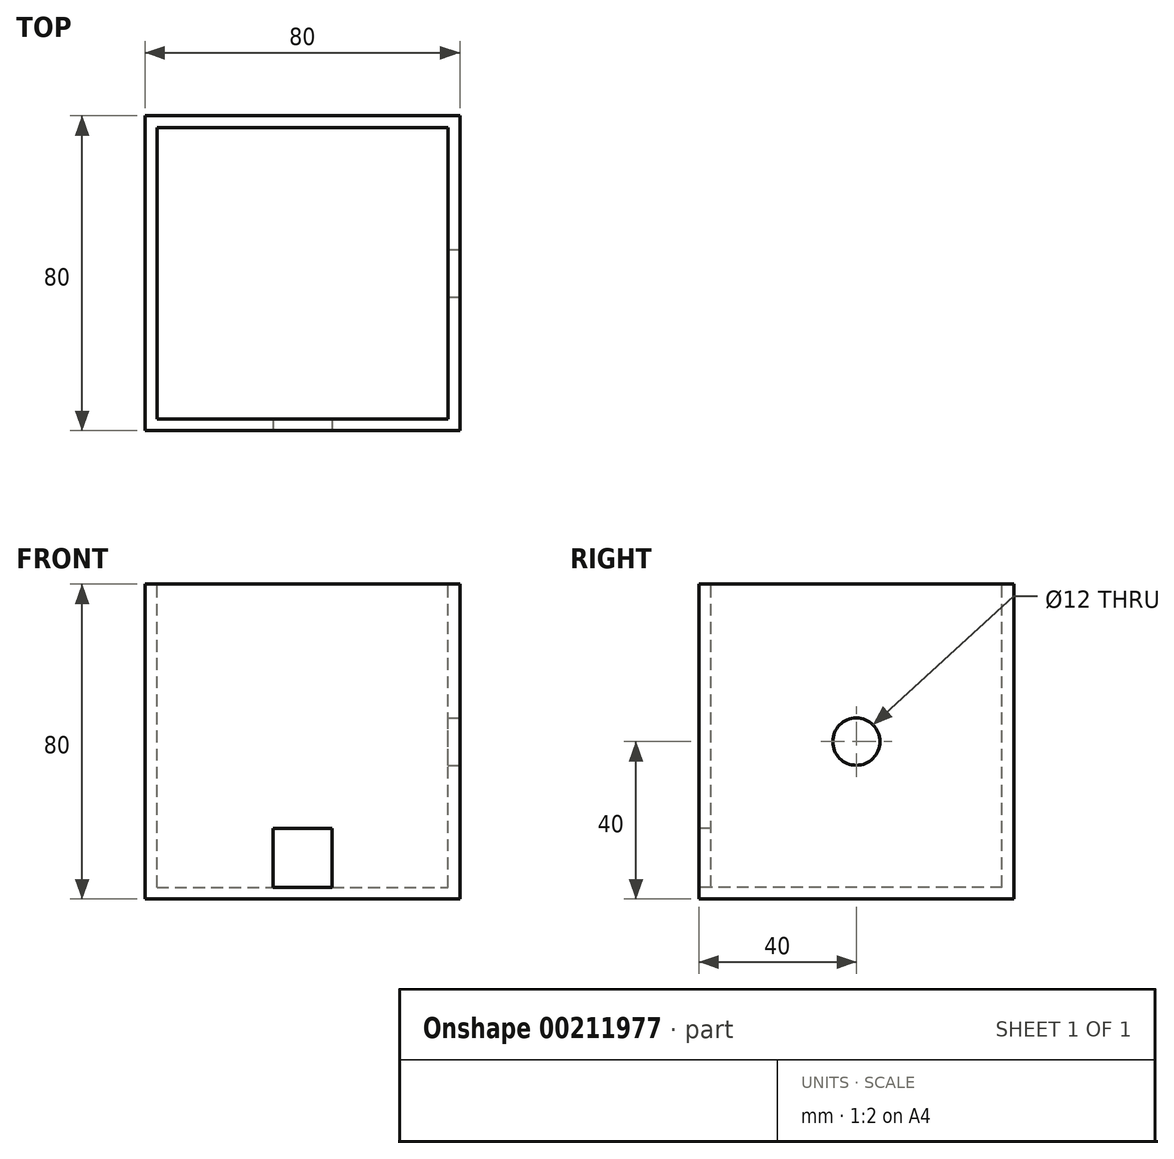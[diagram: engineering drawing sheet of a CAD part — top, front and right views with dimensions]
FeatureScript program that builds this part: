
annotation { "Feature Type Name" : "Feature", "Feature Type Description" : "" }
export const myFeature = defineFeature(function(context is Context, id is Id, definition is map)
    precondition{}
    {
        {
            var Q0;
            Q0=qCreatedBy(makeId("Front.planeOp"),FACE);
            var sketch = newSketch(context, id + "F0", { "sketchPlane" : qUnion([Q0])});
            skLineSegment(sketch, "E0.bottom", {"start": v(-40, -40) * mm, "end": v(40, -40) * mm});
            skLineSegment(sketch, "E0.top", {"start": v(-40, 40) * mm, "end": v(40, 40) * mm});
            skLineSegment(sketch, "E0.left", {"start": v(-40, -40) * mm, "end": v(-40, 40) * mm});
            skLineSegment(sketch, "E0.right", {"start": v(40, -40) * mm, "end": v(40, 40) * mm});
            skPoint(sketch, "E0.middle", {"position": v(0, 0) * mm});
            skSolve(sketch);
        }
        {
            var Q0;
            Q0 = qSketchRegion(id + "F0", true);
            extrude(context, id + "F1", {"entities" : qUnion([Q0]), "depth" : 3 * mm});
        }
        {
            var Q0;
            Q0=makeQuery(id+"F1.opExtrude","CAP_FACE",FACE,{"disambiguationData":[OSD([sQuery(id+"F0.wireOp",EDGE,"E0.bottom"),sQuery(id+"F0.wireOp",EDGE,"E0.top"),sQuery(id+"F0.wireOp",EDGE,"E0.left"),sQuery(id+"F0.wireOp",EDGE,"E0.right")])],"isStart":true});
            var sketch = newSketch(context, id + "F2", { "sketchPlane" : qUnion([Q0])});
            skLineSegment(sketch, "E1.bottom", {"start": v(40, -40) * mm, "end": v(-40, -40) * mm});
            skLineSegment(sketch, "E1.left", {"start": v(40, -40) * mm, "end": v(40, 40) * mm});
            skLineSegment(sketch, "E1.right", {"start": v(-40, -40) * mm, "end": v(-40, 40) * mm});
            skPoint(sketch, "E1.middle", {"position": v(0, 0) * mm});
            skLineSegment(sketch, "E2.bottom", {"start": v(37, -37) * mm, "end": v(-37, -37) * mm});
            skLineSegment(sketch, "E2.left", {"start": v(37, -37) * mm, "end": v(37, 37) * mm});
            skLineSegment(sketch, "E2.right", {"start": v(-37, -37) * mm, "end": v(-37, 37) * mm});
            skLineSegment(sketch, "E3", {"start": v(-37, 37) * mm, "end": v(-37, 40) * mm});
            skLineSegment(sketch, "E4", {"start": v(37, 37) * mm, "end": v(37, 40) * mm});
            skSolve(sketch);
        }
        {
            var Q0;
            Q0 = qSketchRegion(id + "F2", true);
            var Q1;
            Q1=makeQuery(id+"F2.imprint","IMPRINT",FACE,{"disambiguationData":[TD([[makeQuery(id+"F2.imprint","IMPRINT",EDGE,{"derivedFrom":sQuery(id+"F2.wireOp",EDGE,"E1.bottom")}),-1.0]])]});
            extrude(context, id + "F3", {"entities" : qUnion([Q0, Q1]), "operationType" : NewBodyOperationType.ADD, "depth" : (80 - 6) * mm});
        }
        {
            var Q0;
            Q0=makeQuery(id+"F3.opExtrude","CAP_FACE",FACE,{"disambiguationData":[OSD([sQuery(id+"F0.wireOp",EDGE,"E0.top"),sQuery(id+"F2.wireOp",EDGE,"E1.bottom"),sQuery(id+"F2.wireOp",EDGE,"E1.left"),sQuery(id+"F2.wireOp",EDGE,"E1.right"),sQuery(id+"F2.wireOp",EDGE,"E2.bottom"),sQuery(id+"F2.wireOp",EDGE,"E2.left"),sQuery(id+"F2.wireOp",EDGE,"E2.right"),sQuery(id+"F2.wireOp",EDGE,"E3"),sQuery(id+"F2.wireOp",EDGE,"E4")])],"isStart":false});
            var sketch = newSketch(context, id + "F4", { "sketchPlane" : qUnion([Q0])});
            skLineSegment(sketch, "E5.bottom", {"start": v(-40, -40) * mm, "end": v(40, -40) * mm});
            skLineSegment(sketch, "E5.top", {"start": v(-40, 40) * mm, "end": v(40, 40) * mm});
            skLineSegment(sketch, "E5.left", {"start": v(-40, -40) * mm, "end": v(-40, 40) * mm});
            skLineSegment(sketch, "E5.right", {"start": v(40, -40) * mm, "end": v(40, 40) * mm});
            skPoint(sketch, "E5.middle", {"position": v(0, 0) * mm});
            skSolve(sketch);
        }
        {
            var Q0;
            Q0 = qSketchRegion(id + "F4", true);
            extrude(context, id + "F5", {"entities" : qUnion([Q0]), "operationType" : NewBodyOperationType.ADD, "depth" : 3 * mm});
        }
        {
            var Q0;
            Q0=makeQuery(id+"F5.boolean.opBoolean","MERGE",FACE,{"derivedFrom":[makeQuery(id+"F3.boolean.opBoolean","MERGE",FACE,{"derivedFrom":[makeQuery(id+"F1.opExtrude","SWEPT_FACE",FACE,{"disambiguationData":[OSD([sQuery(id+"F0.wireOp",EDGE,"E0.right")])]}),makeQuery(id+"F3.opExtrude","SWEPT_FACE",FACE,{"disambiguationData":[OSD([sQuery(id+"F2.wireOp",EDGE,"E1.right")])]})]}),makeQuery(id+"F5.opExtrude","SWEPT_FACE",FACE,{"disambiguationData":[OSD([sQuery(id+"F4.wireOp",EDGE,"E5.left")])]})]});
            var sketch = newSketch(context, id + "F6", { "sketchPlane" : qUnion([Q0])});
            skCircle(sketch, "E6", {"center": v(37, 0) * mm, "radius": 6 * mm});
            skLineSegment(sketch, "E7", {"start": v(-12.7, 0) * mm, "end": v(81.8, 0) * mm, "construction": true});
            skLineSegment(sketch, "E8", {"start": v(37, 42.9) * mm, "end": v(37, -43.65) * mm, "construction": true});
            skPoint(sketch, "E8.startSnap0", {"position": v(37, 40) * mm});
            skSolve(sketch);
        }
        {
            var Q0;
            Q0 = qSketchRegion(id + "F6", true);
            extrude(context, id + "F7", {"entities" : qUnion([Q0]), "operationType" : NewBodyOperationType.REMOVE, "oppositeDirection" : true, "depth" : 3 * mm});
        }
        {
            var Q0;
            Q0=makeQuery(id+"F1.opExtrude","CAP_FACE",FACE,{"disambiguationData":[OSD([sQuery(id+"F0.wireOp",EDGE,"E0.bottom"),sQuery(id+"F0.wireOp",EDGE,"E0.top"),sQuery(id+"F0.wireOp",EDGE,"E0.left"),sQuery(id+"F0.wireOp",EDGE,"E0.right")])],"isStart":false});
            var sketch = newSketch(context, id + "F8", { "sketchPlane" : qUnion([Q0])});
            skLineSegment(sketch, "E9", {"start": v(0, 43.25) * mm, "end": v(0, -44.44) * mm, "construction": true});
            skPoint(sketch, "E9.startSnap0", {"position": v(0, 40) * mm});
            skLineSegment(sketch, "E10.bottom", {"start": v(-7.5, -37) * mm, "end": v(7.5, -37) * mm});
            skLineSegment(sketch, "E10.top", {"start": v(-7.5, -22) * mm, "end": v(7.5, -22) * mm});
            skLineSegment(sketch, "E10.left", {"start": v(-7.5, -37) * mm, "end": v(-7.5, -22) * mm});
            skLineSegment(sketch, "E10.right", {"start": v(7.5, -37) * mm, "end": v(7.5, -22) * mm});
            skSolve(sketch);
        }
        {
            var Q0;
            Q0 = qSketchRegion(id + "F8", true);
            extrude(context, id + "F9", {"entities" : qUnion([Q0]), "operationType" : NewBodyOperationType.REMOVE, "oppositeDirection" : true, "depth" : 3 * mm});
        }
    });
